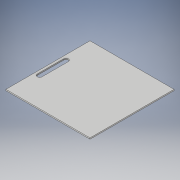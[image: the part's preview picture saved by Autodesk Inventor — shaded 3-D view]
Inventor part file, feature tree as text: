
AUTODESK INVENTOR PART (.ipt)
format: ipt  version: 2019 (Build 230136000, 136)  size: 110,080 bytes
history: native  units: in
note: dims shown in document units (in); Inventor stores cm internally (conversion verified against a paired STEP export)
features: extrude x2, sketch x2
ambient origin geometry x8: Origin, YZ Plane, XZ Plane, XY Plane, X Axis, Y Axis, Z Axis, Center Point
bodies: Solid1 (feature_tree)
feature tree (4):
  extrude  "Extrusion1"  Depth=17.5in
  extrude  "Extrusion3"  Depth=17.5in
  sketch  "Sketch1"  dims[d0=17.5in d1=17.5in]
  sketch  "Sketch2"  dims[d2=0.25in d3=0.0in d8=17.5in d12=1.0in d13=0.5in d14=6.5in d15=5.5in d16=1.0in d17=0.0in]
